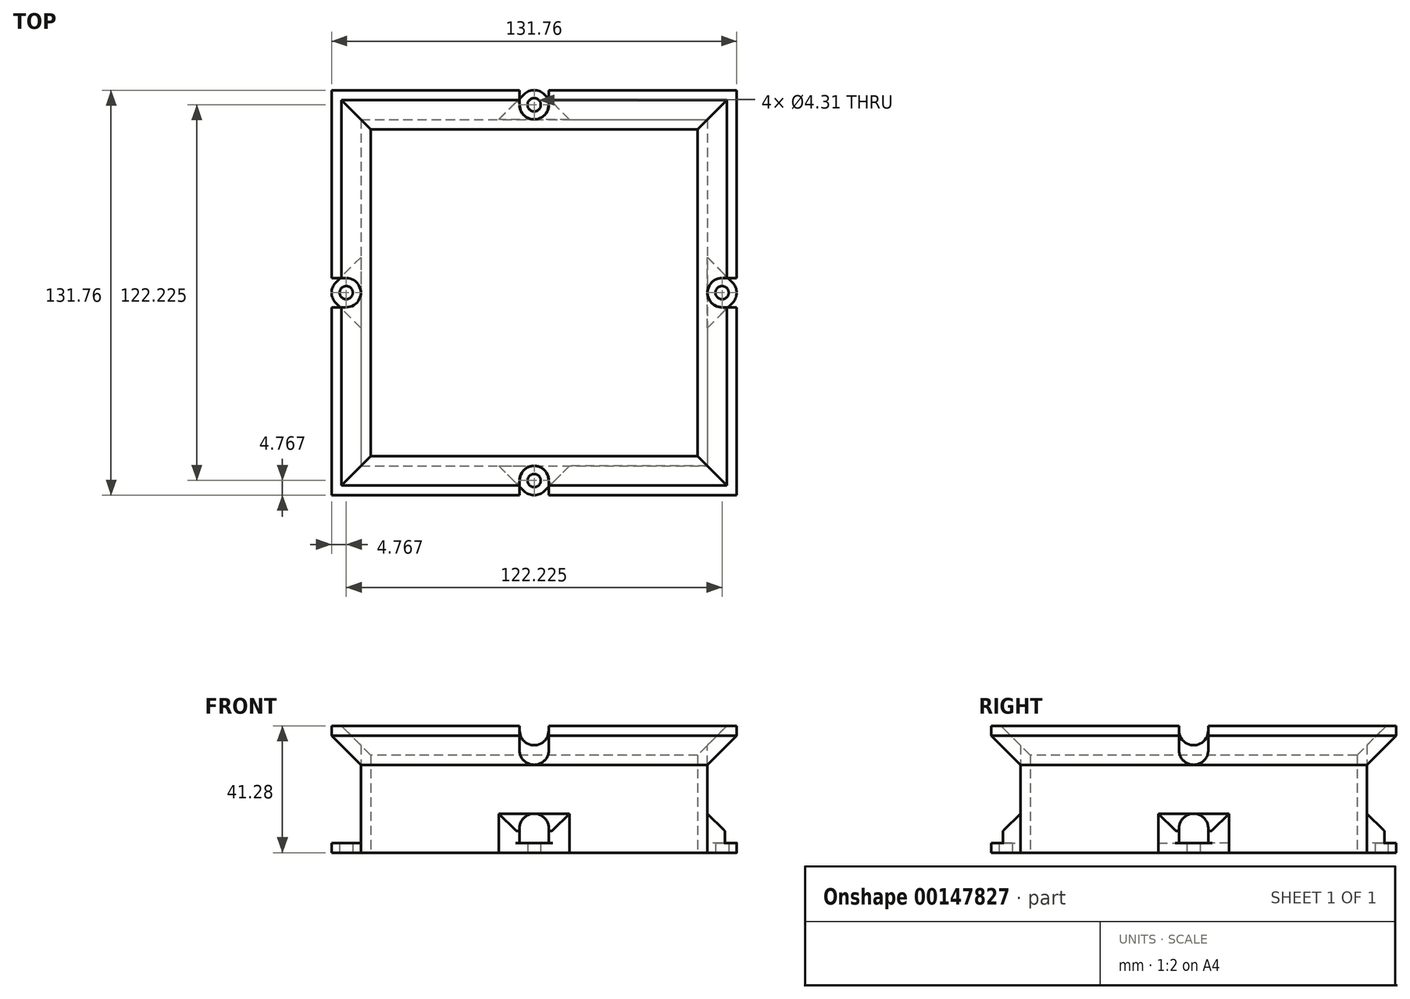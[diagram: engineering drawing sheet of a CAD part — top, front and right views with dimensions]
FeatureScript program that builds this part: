
annotation { "Feature Type Name" : "Feature", "Feature Type Description" : "" }
export const myFeature = defineFeature(function(context is Context, id is Id, definition is map)
    precondition{}
    {
        {
            var Q0;
            Q0=qCreatedBy(makeId("Top.planeOp"),FACE);
            var sketch = newSketch(context, id + "F0", { "sketchPlane" : qUnion([Q0])});
            skLineSegment(sketch, "E0.bottom", {"start": v(53.18, 53.18) * mm, "end": v(-53.18, 53.18) * mm});
            skLineSegment(sketch, "E0.top", {"start": v(53.18, -53.18) * mm, "end": v(-53.18, -53.18) * mm});
            skLineSegment(sketch, "E0.left", {"start": v(53.18, 53.18) * mm, "end": v(53.18, -53.18) * mm});
            skLineSegment(sketch, "E0.right", {"start": v(-53.18, 53.18) * mm, "end": v(-53.18, -53.18) * mm});
            skPoint(sketch, "E0.middle", {"position": v(0, 0) * mm});
            skLineSegment(sketch, "E1", {"start": v(0, 53.18) * mm, "end": v(0, 56.35) * mm, "construction": true});
            skLineSegment(sketch, "E2", {"start": v(53.18, 0) * mm, "end": v(56.35, 0) * mm, "construction": true});
            skLineSegment(sketch, "E3", {"start": v(0, -53.18) * mm, "end": v(0, -56.35) * mm, "construction": true});
            skLineSegment(sketch, "E4", {"start": v(-53.18, 0) * mm, "end": v(-56.35, 0) * mm, "construction": true});
            skLineSegment(sketch, "E5", {"start": v(-56.35, 56.35) * mm, "end": v(-11.5, 56.35) * mm});
            skLineSegment(sketch, "E6", {"start": v(56.35, -11.5) * mm, "end": v(56.35, -56.35) * mm});
            skLineSegment(sketch, "E7", {"start": v(56.35, -56.35) * mm, "end": v(11.5, -56.35) * mm});
            skLineSegment(sketch, "E8", {"start": v(-56.35, 56.35) * mm, "end": v(-56.35, 11.5) * mm});
            skLineSegment(sketch, "E9.bottom", {"start": v(-11.5, 56.35) * mm, "end": v(11.5, 56.35) * mm, "construction": true});
            skLineSegment(sketch, "E9.left", {"start": v(-11.5, 56.35) * mm, "end": v(-3.37, 64.48) * mm});
            skLineSegment(sketch, "E9.right", {"start": v(11.5, 56.35) * mm, "end": v(3.37, 64.48) * mm});
            skArc(sketch, "E10", {"start": v(3.37, 64.48) * mm, "mid": v(0, 65.88) * mm, "end": v(-3.37, 64.48) * mm});
            skLineSegment(sketch, "E11.bottom", {"start": v(-56.35, 11.5) * mm, "end": v(-64.48, 3.37) * mm});
            skLineSegment(sketch, "E11.top", {"start": v(-56.35, -11.5) * mm, "end": v(-64.48, -3.37) * mm});
            skLineSegment(sketch, "E11.left", {"start": v(-56.35, 11.5) * mm, "end": v(-56.35, -11.5) * mm, "construction": true});
            skLineSegment(sketch, "E12.bottom", {"start": v(56.35, 11.5) * mm, "end": v(64.48, 3.37) * mm});
            skLineSegment(sketch, "E12.top", {"start": v(56.35, -11.5) * mm, "end": v(64.48, -3.37) * mm});
            skLineSegment(sketch, "E12.left", {"start": v(56.35, 11.5) * mm, "end": v(56.35, -11.5) * mm, "construction": true});
            skLineSegment(sketch, "E13.top", {"start": v(11.5, -56.35) * mm, "end": v(-11.5, -56.35) * mm, "construction": true});
            skLineSegment(sketch, "E13.left", {"start": v(3.37, -64.48) * mm, "end": v(11.5, -56.35) * mm});
            skLineSegment(sketch, "E13.right", {"start": v(-3.37, -64.48) * mm, "end": v(-11.5, -56.35) * mm});
            skLineSegment(sketch, "E14.bottom", {"start": v(11.5, 56.35) * mm, "end": v(56.35, 56.35) * mm});
            skLineSegment(sketch, "E14.right", {"start": v(56.35, 56.35) * mm, "end": v(56.35, 11.5) * mm});
            skLineSegment(sketch, "E15.top", {"start": v(-56.35, -56.35) * mm, "end": v(-11.5, -56.35) * mm});
            skLineSegment(sketch, "E15.left", {"start": v(-56.35, -11.5) * mm, "end": v(-56.35, -56.35) * mm});
            skArc(sketch, "E16", {"start": v(-64.48, 3.37) * mm, "mid": v(-65.88, 0) * mm, "end": v(-64.48, -3.37) * mm});
            skArc(sketch, "E17", {"start": v(-3.37, -64.48) * mm, "mid": v(0, -65.88) * mm, "end": v(3.37, -64.48) * mm});
            skArc(sketch, "E18", {"start": v(64.48, -3.37) * mm, "mid": v(65.88, 0) * mm, "end": v(64.48, 3.37) * mm});
            skCircle(sketch, "E19", {"center": v(0, 61.11) * mm, "radius": 2.15 * mm, "construction": true});
            skCircle(sketch, "E20", {"center": v(-61.11, 0) * mm, "radius": 2.15 * mm, "construction": true});
            skCircle(sketch, "E21", {"center": v(0, -61.11) * mm, "radius": 2.15 * mm, "construction": true});
            skCircle(sketch, "E22", {"center": v(61.11, 0) * mm, "radius": 2.15 * mm, "construction": true});
            skLineSegment(sketch, "E23", {"start": v(-61.11, 0) * mm, "end": v(-56.35, 0) * mm, "construction": true});
            skLineSegment(sketch, "E24", {"start": v(0, -61.11) * mm, "end": v(0, -56.35) * mm, "construction": true});
            skLineSegment(sketch, "E25", {"start": v(61.11, 0) * mm, "end": v(56.35, 0) * mm, "construction": true});
            skLineSegment(sketch, "E26", {"start": v(0, 56.35) * mm, "end": v(0, 61.11) * mm, "construction": true});
            skSolve(sketch);
        }
        {
            var Q0;
            Q0=qSketchRegion(id+"F0",true);
            extrude(context, id + "F1", {"entities" : qUnion([Q0]), "depth" : 3.17 * mm});
        }
        {
            var Q0;
            Q0=makeQuery(id+"F1.opExtrude","CAP_FACE",FACE,{"disambiguationData":[OSD([sQuery(id+"F0.wireOp",EDGE,"E0.bottom"),sQuery(id+"F0.wireOp",EDGE,"E0.top"),sQuery(id+"F0.wireOp",EDGE,"E0.left"),sQuery(id+"F0.wireOp",EDGE,"E0.right"),sQuery(id+"F0.wireOp",EDGE,"E5"),sQuery(id+"F0.wireOp",EDGE,"E6"),sQuery(id+"F0.wireOp",EDGE,"E7"),sQuery(id+"F0.wireOp",EDGE,"E8"),sQuery(id+"F0.wireOp",EDGE,"E9.left"),sQuery(id+"F0.wireOp",EDGE,"E9.right"),sQuery(id+"F0.wireOp",EDGE,"E10"),sQuery(id+"F0.wireOp",EDGE,"E11.bottom"),sQuery(id+"F0.wireOp",EDGE,"E11.top"),sQuery(id+"F0.wireOp",EDGE,"E12.bottom"),sQuery(id+"F0.wireOp",EDGE,"E12.top"),sQuery(id+"F0.wireOp",EDGE,"E13.left"),sQuery(id+"F0.wireOp",EDGE,"E13.right"),sQuery(id+"F0.wireOp",EDGE,"E14.bottom"),sQuery(id+"F0.wireOp",EDGE,"E14.right"),sQuery(id+"F0.wireOp",EDGE,"E15.top"),sQuery(id+"F0.wireOp",EDGE,"E15.left"),sQuery(id+"F0.wireOp",EDGE,"E16"),sQuery(id+"F0.wireOp",EDGE,"E17"),sQuery(id+"F0.wireOp",EDGE,"E18"),sQuery(id+"F0.wireOp",EDGE,"E19"),sQuery(id+"F0.wireOp",EDGE,"E20"),sQuery(id+"F0.wireOp",EDGE,"E21"),sQuery(id+"F0.wireOp",EDGE,"E22")])],"isStart":false});
            var sketch = newSketch(context, id + "F2", { "sketchPlane" : qUnion([Q0])});
            skLineSegment(sketch, "E27.bottom", {"start": v(-56.35, 56.35) * mm, "end": v(56.35, 56.35) * mm});
            skLineSegment(sketch, "E27.top", {"start": v(-56.35, -56.35) * mm, "end": v(56.35, -56.35) * mm});
            skLineSegment(sketch, "E27.left", {"start": v(-56.35, 56.35) * mm, "end": v(-56.35, -56.35) * mm});
            skLineSegment(sketch, "E27.right", {"start": v(56.35, 56.35) * mm, "end": v(56.35, -56.35) * mm});
            skLineSegment(sketch, "E28.bottom", {"start": v(53.18, -53.18) * mm, "end": v(-53.18, -53.18) * mm});
            skLineSegment(sketch, "E28.top", {"start": v(53.18, 53.18) * mm, "end": v(-53.18, 53.18) * mm});
            skLineSegment(sketch, "E28.left", {"start": v(53.18, -53.18) * mm, "end": v(53.18, 53.18) * mm});
            skLineSegment(sketch, "E28.right", {"start": v(-53.18, -53.18) * mm, "end": v(-53.18, 53.18) * mm});
            skSolve(sketch);
        }
        {
            var Q0;
            Q0=qSketchRegion(id+"F2",true);
            extrude(context, id + "F3", {"entities" : qUnion([Q0]), "operationType" : NewBodyOperationType.ADD, "depth" : 25.4 * mm});
        }
        {
            var Q0;
            Q0=makeQuery(id+"F3.opExtrude","CAP_FACE",FACE,{"disambiguationData":[OSD([sQuery(id+"F2.wireOp",EDGE,"E27.bottom"),sQuery(id+"F2.wireOp",EDGE,"E27.top"),sQuery(id+"F2.wireOp",EDGE,"E27.left"),sQuery(id+"F2.wireOp",EDGE,"E27.right"),sQuery(id+"F2.wireOp",EDGE,"E28.bottom"),sQuery(id+"F2.wireOp",EDGE,"E28.top"),sQuery(id+"F2.wireOp",EDGE,"E28.left"),sQuery(id+"F2.wireOp",EDGE,"E28.right")])],"isStart":false});
            var sketch = newSketch(context, id + "F4", { "sketchPlane" : qUnion([Q0])});
            skLineSegment(sketch, "E29.bottom", {"start": v(-53.18, 53.18) * mm, "end": v(53.18, 53.18) * mm});
            skLineSegment(sketch, "E29.top", {"start": v(-53.18, -53.18) * mm, "end": v(53.18, -53.18) * mm});
            skLineSegment(sketch, "E29.left", {"start": v(-53.18, 53.18) * mm, "end": v(-53.18, -53.18) * mm});
            skLineSegment(sketch, "E29.right", {"start": v(53.18, 53.18) * mm, "end": v(53.18, -53.18) * mm});
            skLineSegment(sketch, "E30", {"start": v(0, 53.18) * mm, "end": v(0, -53.18) * mm, "construction": true});
            skLineSegment(sketch, "E31.bottom", {"start": v(65.88, 65.88) * mm, "end": v(-65.88, 65.88) * mm});
            skLineSegment(sketch, "E31.top", {"start": v(65.88, -65.88) * mm, "end": v(-65.88, -65.88) * mm});
            skLineSegment(sketch, "E31.left", {"start": v(65.88, 65.88) * mm, "end": v(65.88, -65.88) * mm});
            skLineSegment(sketch, "E31.right", {"start": v(-65.88, 65.88) * mm, "end": v(-65.88, -65.88) * mm});
            skPoint(sketch, "E31.middle", {"position": v(0, 0) * mm});
            skLineSegment(sketch, "E32", {"start": v(56.35, 56.35) * mm, "end": v(56.35, 65.88) * mm, "construction": true});
            skLineSegment(sketch, "E33", {"start": v(56.35, 56.35) * mm, "end": v(65.88, 56.35) * mm, "construction": true});
            skSolve(sketch);
        }
        {
            var Q0;
            Q0=qSketchRegion(id+"F4",true);
            extrude(context, id + "F5", {"entities" : qUnion([Q0]), "operationType" : NewBodyOperationType.ADD, "depth" : 12.7 * mm});
        }
        {
            var Q0;
            Q0=makeQuery(id+"F5.opExtrude","CAP_EDGE",EDGE,{"disambiguationData":[OSD([sQuery(id+"F4.wireOp",EDGE,"E31.right")])],"isStart":true});
            var Q1;
            Q1=makeQuery(id+"F5.opExtrude","CAP_EDGE",EDGE,{"disambiguationData":[OSD([sQuery(id+"F4.wireOp",EDGE,"E31.top")])],"isStart":true});
            var Q2;
            Q2=makeQuery(id+"F5.opExtrude","CAP_EDGE",EDGE,{"disambiguationData":[OSD([sQuery(id+"F4.wireOp",EDGE,"E31.bottom")])],"isStart":true});
            var Q3;
            Q3=makeQuery(id+"F5.opExtrude","CAP_EDGE",EDGE,{"disambiguationData":[OSD([sQuery(id+"F4.wireOp",EDGE,"E31.left")])],"isStart":true});
            var Q4;
            Q4=makeQuery(id+"F5.opExtrude","CAP_EDGE",EDGE,{"disambiguationData":[OSD([sQuery(id+"F4.wireOp",EDGE,"E29.right")])],"isStart":false});
            var Q5;
            Q5=makeQuery(id+"F5.opExtrude","CAP_EDGE",EDGE,{"disambiguationData":[OSD([sQuery(id+"F4.wireOp",EDGE,"E29.top")])],"isStart":false});
            var Q6;
            Q6=makeQuery(id+"F5.opExtrude","CAP_EDGE",EDGE,{"disambiguationData":[OSD([sQuery(id+"F4.wireOp",EDGE,"E29.left")])],"isStart":false});
            var Q7;
            Q7=makeQuery(id+"F5.opExtrude","CAP_EDGE",EDGE,{"disambiguationData":[OSD([sQuery(id+"F4.wireOp",EDGE,"E29.bottom")])],"isStart":false});
            chamfer(context, id + "F6", {"entities" : qUnion([Q0, Q1, Q2, Q3, Q4, Q5, Q6, Q7]), "width" : 9.52 * mm, "tangentPropagation" : true});
        }
        {
            var Q0;
            Q0=makeQuery(id+"F3.opExtrude","CAP_EDGE",EDGE,{"disambiguationData":[OSD([sQuery(id+"F2.wireOp",EDGE,"E27.bottom")])],"isStart":true});
            var Q1;
            Q1=makeQuery(id+"F3.opExtrude","CAP_EDGE",EDGE,{"disambiguationData":[OSD([sQuery(id+"F2.wireOp",EDGE,"E27.left")])],"isStart":true});
            var Q2;
            Q2=makeQuery(id+"F3.opExtrude","CAP_EDGE",EDGE,{"disambiguationData":[OSD([sQuery(id+"F2.wireOp",EDGE,"E27.top")])],"isStart":true});
            var Q3;
            Q3=makeQuery(id+"F3.opExtrude","CAP_EDGE",EDGE,{"disambiguationData":[OSD([sQuery(id+"F2.wireOp",EDGE,"E27.right")])],"isStart":true});
            chamfer(context, id + "F7", {"entities" : qUnion([Q0, Q1, Q2, Q3]), "width" : 9.52 * mm, "tangentPropagation" : true});
        }
        {
            var Q0;
            Q0=makeQuery(id+"F1.opExtrude","CAP_FACE",FACE,{"disambiguationData":[OSD([sQuery(id+"F0.wireOp",EDGE,"E0.bottom"),sQuery(id+"F0.wireOp",EDGE,"E0.top"),sQuery(id+"F0.wireOp",EDGE,"E0.left"),sQuery(id+"F0.wireOp",EDGE,"E0.right"),sQuery(id+"F0.wireOp",EDGE,"E5"),sQuery(id+"F0.wireOp",EDGE,"E6"),sQuery(id+"F0.wireOp",EDGE,"E7"),sQuery(id+"F0.wireOp",EDGE,"E8"),sQuery(id+"F0.wireOp",EDGE,"E9.left"),sQuery(id+"F0.wireOp",EDGE,"E9.right"),sQuery(id+"F0.wireOp",EDGE,"E10"),sQuery(id+"F0.wireOp",EDGE,"E11.bottom"),sQuery(id+"F0.wireOp",EDGE,"E11.top"),sQuery(id+"F0.wireOp",EDGE,"E12.bottom"),sQuery(id+"F0.wireOp",EDGE,"E12.top"),sQuery(id+"F0.wireOp",EDGE,"E13.left"),sQuery(id+"F0.wireOp",EDGE,"E13.right"),sQuery(id+"F0.wireOp",EDGE,"E14.bottom"),sQuery(id+"F0.wireOp",EDGE,"E14.right"),sQuery(id+"F0.wireOp",EDGE,"E15.top"),sQuery(id+"F0.wireOp",EDGE,"E15.left"),sQuery(id+"F0.wireOp",EDGE,"E16"),sQuery(id+"F0.wireOp",EDGE,"E17"),sQuery(id+"F0.wireOp",EDGE,"E18")])],"isStart":true});
            cPlane(context, id + "F8", {"entities" : qUnion([Q0]), "cplaneType" : CPlaneType.OFFSET, "offset" : 3.17 * mm, "oppositeDirection" : true, "width" : 152.4 * mm, "height" : 152.4 * mm});
        }
        {
            var Q0;
            Q0=qCreatedBy(id+"F8.planeOp",FACE);
            var sketch = newSketch(context, id + "F9", { "sketchPlane" : qUnion([Q0])});
            skLineSegment(sketch, "E34.bottom", {"start": v(-65.88, 4.76) * mm, "end": v(-56.35, 4.76) * mm});
            skLineSegment(sketch, "E34.top", {"start": v(-65.88, -4.76) * mm, "end": v(-56.35, -4.76) * mm});
            skLineSegment(sketch, "E34.left", {"start": v(-65.88, 4.76) * mm, "end": v(-65.88, -4.76) * mm});
            skLineSegment(sketch, "E34.right", {"start": v(-56.35, 4.76) * mm, "end": v(-56.35, -4.76) * mm});
            skPoint(sketch, "E34.middle", {"position": v(-61.11, 0) * mm});
            skLineSegment(sketch, "E35.bottom", {"start": v(-4.76, -56.35) * mm, "end": v(4.76, -56.35) * mm});
            skLineSegment(sketch, "E35.top", {"start": v(-4.76, -65.88) * mm, "end": v(4.76, -65.88) * mm});
            skLineSegment(sketch, "E35.left", {"start": v(-4.76, -56.35) * mm, "end": v(-4.76, -65.88) * mm});
            skLineSegment(sketch, "E35.right", {"start": v(4.76, -56.35) * mm, "end": v(4.76, -65.88) * mm});
            skPoint(sketch, "E35.middle", {"position": v(0, -61.11) * mm});
            skLineSegment(sketch, "E36.bottom", {"start": v(56.35, -4.76) * mm, "end": v(65.88, -4.76) * mm});
            skLineSegment(sketch, "E36.top", {"start": v(56.35, 4.76) * mm, "end": v(65.88, 4.76) * mm});
            skLineSegment(sketch, "E36.left", {"start": v(56.35, -4.76) * mm, "end": v(56.35, 4.76) * mm});
            skLineSegment(sketch, "E36.right", {"start": v(65.88, -4.76) * mm, "end": v(65.88, 4.76) * mm});
            skPoint(sketch, "E36.middle", {"position": v(61.11, 0) * mm});
            skLineSegment(sketch, "E37.bottom", {"start": v(4.76, 56.35) * mm, "end": v(-4.76, 56.35) * mm});
            skLineSegment(sketch, "E37.top", {"start": v(4.76, 65.88) * mm, "end": v(-4.76, 65.88) * mm});
            skLineSegment(sketch, "E37.left", {"start": v(4.76, 56.35) * mm, "end": v(4.76, 65.88) * mm});
            skLineSegment(sketch, "E37.right", {"start": v(-4.76, 56.35) * mm, "end": v(-4.76, 65.88) * mm});
            skPoint(sketch, "E37.middle", {"position": v(0, 61.11) * mm});
            skSolve(sketch);
        }
        {
            var Q0;
            Q0=qSketchRegion(id+"F9",true);
            var Q1;
            Q1=makeQuery(id+"F5.opExtrude","CAP_FACE",FACE,{"disambiguationData":[OSD([sQuery(id+"F4.wireOp",EDGE,"E29.bottom"),sQuery(id+"F4.wireOp",EDGE,"E29.top"),sQuery(id+"F4.wireOp",EDGE,"E29.left"),sQuery(id+"F4.wireOp",EDGE,"E29.right"),sQuery(id+"F4.wireOp",EDGE,"E31.bottom"),sQuery(id+"F4.wireOp",EDGE,"E31.top"),sQuery(id+"F4.wireOp",EDGE,"E31.left"),sQuery(id+"F4.wireOp",EDGE,"E31.right")])],"isStart":false});
            extrude(context, id + "F10", {"entities" : qUnion([Q0]), "operationType" : NewBodyOperationType.REMOVE, "endBound" : BoundingType.UP_TO_SURFACE, "oppositeDirection" : true, "endBoundEntityFace" : qUnion([Q1]), "depth" : 25.4 * mm});
        }
        {
            var Q0;
            Q0=makeQuery(id+"F10.boolean.opBoolean","COPY",EDGE,{"disambiguationData":[OD(1.0)],"derivedFrom":makeQuery(id+"F10.opExtrude","SWEPT_EDGE",EDGE,{"disambiguationData":[OSD([sQuery(id+"F9.wireOp",EDGE,"E37.bottom"),sQuery(id+"F9.wireOp",EDGE,"E37.left")])]})});
            var Q1;
            Q1=makeQuery(id+"F10.boolean.opBoolean","COPY",EDGE,{"disambiguationData":[OD(1.0)],"derivedFrom":makeQuery(id+"F10.opExtrude","SWEPT_EDGE",EDGE,{"disambiguationData":[OSD([sQuery(id+"F9.wireOp",EDGE,"E37.bottom"),sQuery(id+"F9.wireOp",EDGE,"E37.right")])]})});
            var Q2;
            Q2=makeQuery(id+"F10.boolean.opBoolean","COPY",EDGE,{"disambiguationData":[OD(0.0)],"derivedFrom":makeQuery(id+"F10.opExtrude","SWEPT_EDGE",EDGE,{"disambiguationData":[OSD([sQuery(id+"F9.wireOp",EDGE,"E37.bottom"),sQuery(id+"F9.wireOp",EDGE,"E37.right")])]})});
            var Q3;
            Q3=makeQuery(id+"F10.boolean.opBoolean","COPY",EDGE,{"disambiguationData":[OD(0.0)],"derivedFrom":makeQuery(id+"F10.opExtrude","SWEPT_EDGE",EDGE,{"disambiguationData":[OSD([sQuery(id+"F9.wireOp",EDGE,"E37.bottom"),sQuery(id+"F9.wireOp",EDGE,"E37.left")])]})});
            var Q4;
            Q4=makeQuery(id+"F10.boolean.opBoolean","COPY",EDGE,{"disambiguationData":[OD(0.0)],"derivedFrom":makeQuery(id+"F10.opExtrude","SWEPT_EDGE",EDGE,{"disambiguationData":[OSD([sQuery(id+"F9.wireOp",EDGE,"E34.bottom"),sQuery(id+"F9.wireOp",EDGE,"E34.right")])]})});
            var Q5;
            Q5=makeQuery(id+"F10.boolean.opBoolean","COPY",EDGE,{"disambiguationData":[OD(0.0)],"derivedFrom":makeQuery(id+"F10.opExtrude","SWEPT_EDGE",EDGE,{"disambiguationData":[OSD([sQuery(id+"F9.wireOp",EDGE,"E34.top"),sQuery(id+"F9.wireOp",EDGE,"E34.right")])]})});
            var Q6;
            Q6=makeQuery(id+"F10.boolean.opBoolean","COPY",EDGE,{"disambiguationData":[OD(1.0)],"derivedFrom":makeQuery(id+"F10.opExtrude","SWEPT_EDGE",EDGE,{"disambiguationData":[OSD([sQuery(id+"F9.wireOp",EDGE,"E34.top"),sQuery(id+"F9.wireOp",EDGE,"E34.right")])]})});
            var Q7;
            Q7=makeQuery(id+"F10.boolean.opBoolean","COPY",EDGE,{"disambiguationData":[OD(1.0)],"derivedFrom":makeQuery(id+"F10.opExtrude","SWEPT_EDGE",EDGE,{"disambiguationData":[OSD([sQuery(id+"F9.wireOp",EDGE,"E34.bottom"),sQuery(id+"F9.wireOp",EDGE,"E34.right")])]})});
            var Q8;
            Q8=makeQuery(id+"F10.boolean.opBoolean","COPY",EDGE,{"disambiguationData":[OD(1.0)],"derivedFrom":makeQuery(id+"F10.opExtrude","SWEPT_EDGE",EDGE,{"disambiguationData":[OSD([sQuery(id+"F9.wireOp",EDGE,"E35.bottom"),sQuery(id+"F9.wireOp",EDGE,"E35.left")])]})});
            var Q9;
            Q9=makeQuery(id+"F10.boolean.opBoolean","COPY",EDGE,{"disambiguationData":[OD(0.0)],"derivedFrom":makeQuery(id+"F10.opExtrude","SWEPT_EDGE",EDGE,{"disambiguationData":[OSD([sQuery(id+"F9.wireOp",EDGE,"E35.bottom"),sQuery(id+"F9.wireOp",EDGE,"E35.left")])]})});
            var Q10;
            Q10=makeQuery(id+"F10.boolean.opBoolean","COPY",EDGE,{"disambiguationData":[OD(1.0)],"derivedFrom":makeQuery(id+"F10.opExtrude","SWEPT_EDGE",EDGE,{"disambiguationData":[OSD([sQuery(id+"F9.wireOp",EDGE,"E35.bottom"),sQuery(id+"F9.wireOp",EDGE,"E35.right")])]})});
            var Q11;
            Q11=makeQuery(id+"F10.boolean.opBoolean","COPY",EDGE,{"disambiguationData":[OD(0.0)],"derivedFrom":makeQuery(id+"F10.opExtrude","SWEPT_EDGE",EDGE,{"disambiguationData":[OSD([sQuery(id+"F9.wireOp",EDGE,"E35.bottom"),sQuery(id+"F9.wireOp",EDGE,"E35.right")])]})});
            var Q12;
            Q12=makeQuery(id+"F10.boolean.opBoolean","COPY",EDGE,{"disambiguationData":[OD(0.0)],"derivedFrom":makeQuery(id+"F10.opExtrude","SWEPT_EDGE",EDGE,{"disambiguationData":[OSD([sQuery(id+"F9.wireOp",EDGE,"E36.top"),sQuery(id+"F9.wireOp",EDGE,"E36.left")])]})});
            var Q13;
            Q13=makeQuery(id+"F10.boolean.opBoolean","COPY",EDGE,{"disambiguationData":[OD(1.0)],"derivedFrom":makeQuery(id+"F10.opExtrude","SWEPT_EDGE",EDGE,{"disambiguationData":[OSD([sQuery(id+"F9.wireOp",EDGE,"E36.top"),sQuery(id+"F9.wireOp",EDGE,"E36.left")])]})});
            var Q14;
            Q14=makeQuery(id+"F10.boolean.opBoolean","COPY",EDGE,{"disambiguationData":[OD(1.0)],"derivedFrom":makeQuery(id+"F10.opExtrude","SWEPT_EDGE",EDGE,{"disambiguationData":[OSD([sQuery(id+"F9.wireOp",EDGE,"E36.bottom"),sQuery(id+"F9.wireOp",EDGE,"E36.left")])]})});
            var Q15;
            Q15=makeQuery(id+"F10.boolean.opBoolean","COPY",EDGE,{"disambiguationData":[OD(0.0)],"derivedFrom":makeQuery(id+"F10.opExtrude","SWEPT_EDGE",EDGE,{"disambiguationData":[OSD([sQuery(id+"F9.wireOp",EDGE,"E36.bottom"),sQuery(id+"F9.wireOp",EDGE,"E36.left")])]})});
            fillet(context, id + "F11", {"entities" : qUnion([Q0, Q1, Q2, Q3, Q4, Q5, Q6, Q7, Q8, Q9, Q10, Q11, Q12, Q13, Q14, Q15]), "radius" : 4.76 * mm, "tangentPropagation" : true, "allowEdgeOverflow" : false});
        }
        {
            var Q0;
            Q0=makeQuery(id+"F10.boolean.opBoolean","INTERSECT",EDGE,{"derivedFrom":[makeQuery(id+"F1.opExtrude","SWEPT_FACE",FACE,{"disambiguationData":[OSD([sQuery(id+"F0.wireOp",EDGE,"E12.top")])]}),makeQuery(id+"F10.opExtrude","SWEPT_FACE",FACE,{"disambiguationData":[OSD([sQuery(id+"F9.wireOp",EDGE,"E36.top")])]})]});
            var Q1;
            Q1=makeQuery(id+"F10.boolean.opBoolean","INTERSECT",EDGE,{"derivedFrom":[makeQuery(id+"F1.opExtrude","SWEPT_FACE",FACE,{"disambiguationData":[OSD([sQuery(id+"F0.wireOp",EDGE,"E12.bottom")])]}),makeQuery(id+"F10.opExtrude","SWEPT_FACE",FACE,{"disambiguationData":[OSD([sQuery(id+"F9.wireOp",EDGE,"E36.bottom")])]})]});
            var Q2;
            Q2=makeQuery(id+"F10.boolean.opBoolean","INTERSECT",EDGE,{"derivedFrom":[makeQuery(id+"F1.opExtrude","SWEPT_FACE",FACE,{"disambiguationData":[OSD([sQuery(id+"F0.wireOp",EDGE,"E9.right")])]}),makeQuery(id+"F10.opExtrude","SWEPT_FACE",FACE,{"disambiguationData":[OSD([sQuery(id+"F9.wireOp",EDGE,"E35.right")])]})]});
            var Q3;
            Q3=makeQuery(id+"F10.boolean.opBoolean","INTERSECT",EDGE,{"derivedFrom":[makeQuery(id+"F1.opExtrude","SWEPT_FACE",FACE,{"disambiguationData":[OSD([sQuery(id+"F0.wireOp",EDGE,"E9.left")])]}),makeQuery(id+"F10.opExtrude","SWEPT_FACE",FACE,{"disambiguationData":[OSD([sQuery(id+"F9.wireOp",EDGE,"E35.left")])]})]});
            var Q4;
            Q4=makeQuery(id+"F10.boolean.opBoolean","INTERSECT",EDGE,{"derivedFrom":[makeQuery(id+"F1.opExtrude","SWEPT_FACE",FACE,{"disambiguationData":[OSD([sQuery(id+"F0.wireOp",EDGE,"E11.top")])]}),makeQuery(id+"F10.opExtrude","SWEPT_FACE",FACE,{"disambiguationData":[OSD([sQuery(id+"F9.wireOp",EDGE,"E34.bottom")])]})]});
            var Q5;
            Q5=makeQuery(id+"F10.boolean.opBoolean","INTERSECT",EDGE,{"derivedFrom":[makeQuery(id+"F1.opExtrude","SWEPT_FACE",FACE,{"disambiguationData":[OSD([sQuery(id+"F0.wireOp",EDGE,"E11.bottom")])]}),makeQuery(id+"F10.opExtrude","SWEPT_FACE",FACE,{"disambiguationData":[OSD([sQuery(id+"F9.wireOp",EDGE,"E34.top")])]})]});
            var Q6;
            Q6=makeQuery(id+"F10.boolean.opBoolean","INTERSECT",EDGE,{"derivedFrom":[makeQuery(id+"F1.opExtrude","SWEPT_FACE",FACE,{"disambiguationData":[OSD([sQuery(id+"F0.wireOp",EDGE,"E13.right")])]}),makeQuery(id+"F10.opExtrude","SWEPT_FACE",FACE,{"disambiguationData":[OSD([sQuery(id+"F9.wireOp",EDGE,"E37.right")])]})]});
            var Q7;
            Q7=makeQuery(id+"F10.boolean.opBoolean","INTERSECT",EDGE,{"derivedFrom":[makeQuery(id+"F1.opExtrude","SWEPT_FACE",FACE,{"disambiguationData":[OSD([sQuery(id+"F0.wireOp",EDGE,"E13.left")])]}),makeQuery(id+"F10.opExtrude","SWEPT_FACE",FACE,{"disambiguationData":[OSD([sQuery(id+"F9.wireOp",EDGE,"E37.left")])]})]});
            fillet(context, id + "F12", {"entities" : qUnion([Q0, Q1, Q2, Q3, Q4, Q5, Q6, Q7]), "radius" : 0.76 * mm, "tangentPropagation" : true, "allowEdgeOverflow" : false});
        }
        {
            var Q0;
            Q0=makeQuery(id+"F1.opExtrude","CAP_FACE",FACE,{"disambiguationData":[OSD([sQuery(id+"F0.wireOp",EDGE,"E0.bottom"),sQuery(id+"F0.wireOp",EDGE,"E0.top"),sQuery(id+"F0.wireOp",EDGE,"E0.left"),sQuery(id+"F0.wireOp",EDGE,"E0.right"),sQuery(id+"F0.wireOp",EDGE,"E5"),sQuery(id+"F0.wireOp",EDGE,"E6"),sQuery(id+"F0.wireOp",EDGE,"E7"),sQuery(id+"F0.wireOp",EDGE,"E8"),sQuery(id+"F0.wireOp",EDGE,"E9.left"),sQuery(id+"F0.wireOp",EDGE,"E9.right"),sQuery(id+"F0.wireOp",EDGE,"E10"),sQuery(id+"F0.wireOp",EDGE,"E11.bottom"),sQuery(id+"F0.wireOp",EDGE,"E11.top"),sQuery(id+"F0.wireOp",EDGE,"E12.bottom"),sQuery(id+"F0.wireOp",EDGE,"E12.top"),sQuery(id+"F0.wireOp",EDGE,"E13.left"),sQuery(id+"F0.wireOp",EDGE,"E13.right"),sQuery(id+"F0.wireOp",EDGE,"E14.bottom"),sQuery(id+"F0.wireOp",EDGE,"E14.right"),sQuery(id+"F0.wireOp",EDGE,"E15.top"),sQuery(id+"F0.wireOp",EDGE,"E15.left"),sQuery(id+"F0.wireOp",EDGE,"E16"),sQuery(id+"F0.wireOp",EDGE,"E17"),sQuery(id+"F0.wireOp",EDGE,"E18")])],"isStart":true});
            var sketch = newSketch(context, id + "F13", { "sketchPlane" : qUnion([Q0])});
            skCircle(sketch, "E38", {"center": v(0, 61.11) * mm, "radius": 2.15 * mm});
            skCircle(sketch, "E39", {"center": v(-61.11, 0) * mm, "radius": 2.15 * mm});
            skCircle(sketch, "E40", {"center": v(61.11, 0) * mm, "radius": 2.15 * mm});
            skCircle(sketch, "E41", {"center": v(0, -61.11) * mm, "radius": 2.15 * mm});
            skSolve(sketch);
        }
        {
            var Q0;
            Q0=qSketchRegion(id+"F13",true);
            var Q1;
            Q1=makeQuery(id+"F10.boolean.opBoolean","COPY",FACE,{"derivedFrom":makeQuery(id+"F10.opExtrude","CAP_FACE",FACE,{"disambiguationData":[OSD([sQuery(id+"F9.wireOp",EDGE,"E37.bottom"),sQuery(id+"F9.wireOp",EDGE,"E37.top"),sQuery(id+"F9.wireOp",EDGE,"E37.left"),sQuery(id+"F9.wireOp",EDGE,"E37.right")])],"isStart":true})});
            extrude(context, id + "F14", {"entities" : qUnion([Q0]), "operationType" : NewBodyOperationType.REMOVE, "endBound" : BoundingType.UP_TO_SURFACE, "oppositeDirection" : true, "endBoundEntityFace" : qUnion([Q1]), "depth" : 25.4 * mm});
        }
    });
